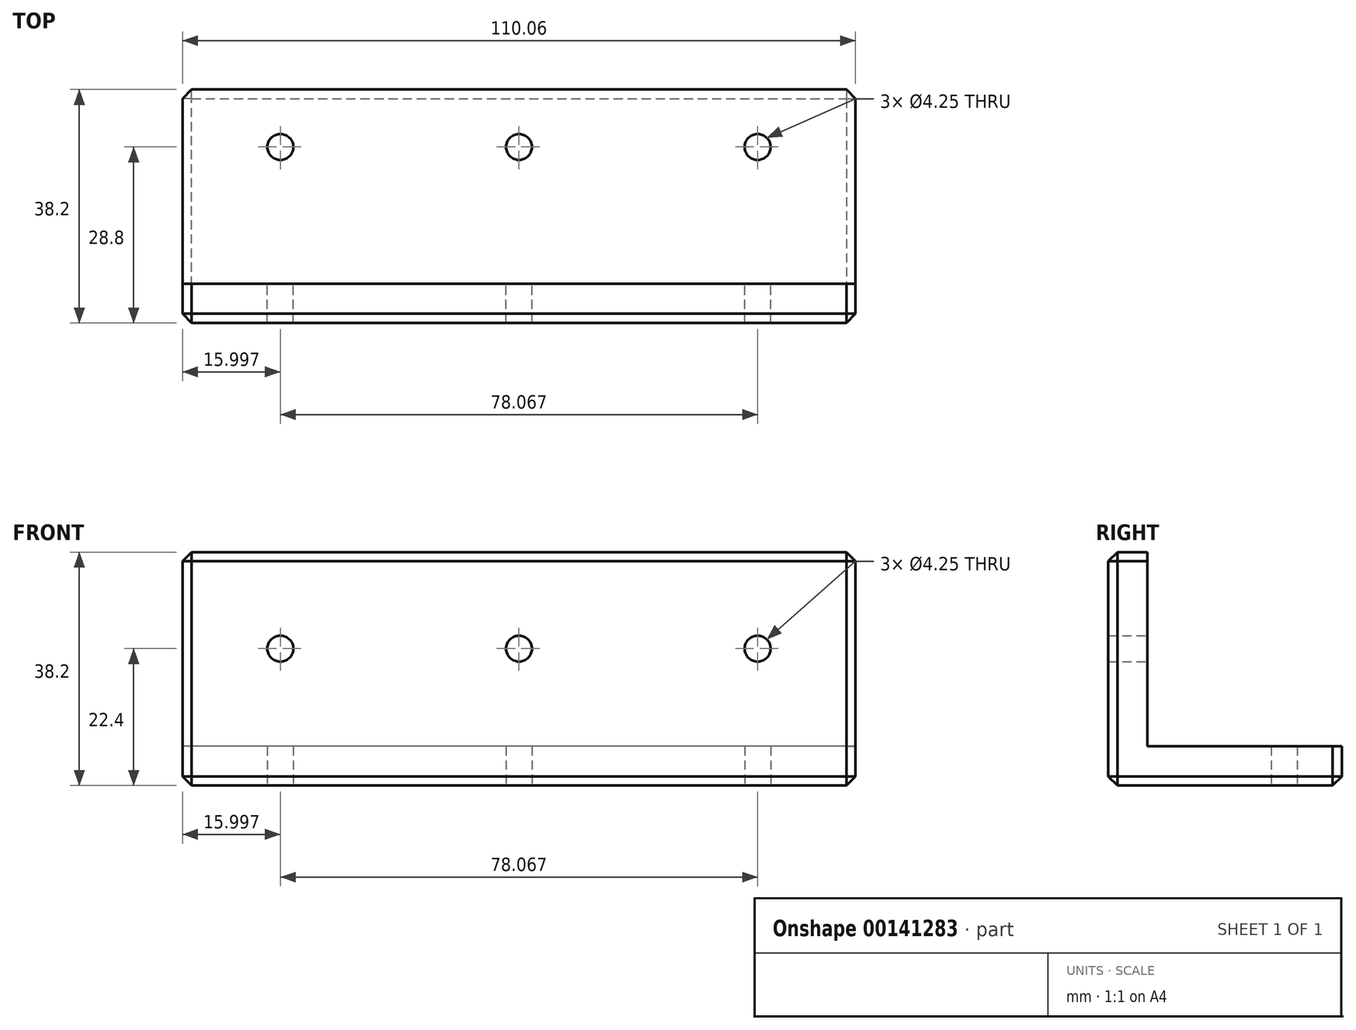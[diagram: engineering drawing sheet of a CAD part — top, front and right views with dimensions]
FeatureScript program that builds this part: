
annotation { "Feature Type Name" : "Feature", "Feature Type Description" : "" }
export const myFeature = defineFeature(function(context is Context, id is Id, definition is map)
    precondition{}
    {
        {
            var Q0;
            Q0=qCreatedBy(makeId("Top.planeOp"),FACE);
            var sketch = newSketch(context, id + "F0", { "sketchPlane" : qUnion([Q0])});
            skLineSegment(sketch, "E0.bottom", {"start": v(55.03, -15.9) * mm, "end": v(-55.03, -15.9) * mm});
            skLineSegment(sketch, "E0.top", {"start": v(55.03, 15.9) * mm, "end": v(-55.03, 15.9) * mm});
            skLineSegment(sketch, "E0.left", {"start": v(55.03, -15.9) * mm, "end": v(55.03, 15.9) * mm});
            skLineSegment(sketch, "E0.right", {"start": v(-55.03, -15.9) * mm, "end": v(-55.03, 15.9) * mm});
            skPoint(sketch, "E0.middle", {"position": v(0, 0) * mm});
            skLineSegment(sketch, "E1", {"start": v(-55.03, -9.5) * mm, "end": v(55.03, -9.5) * mm, "construction": true});
            skCircle(sketch, "E2", {"center": v(0, 6.5) * mm, "radius": 2.12 * mm});
            skCircle(sketch, "E3", {"center": v(-39.03, 6.5) * mm, "radius": 2.12 * mm});
            skCircle(sketch, "E4.MirrorC", {"center": v(39.03, 6.5) * mm, "radius": 2.12 * mm});
            skSolve(sketch);
        }
        {
            var Q0;
            Q0 = qSketchRegion(id + "F0", true);
            extrude(context, id + "F1", {"entities" : qUnion([Q0]), "depth" : 6.4 * mm});
        }
        {
            var Q0;
            Q0=makeQuery(id+"F1.opExtrude","SWEPT_FACE",FACE,{"disambiguationData":[OSD([sQuery(id+"F0.wireOp",EDGE,"E0.bottom")])]});
            var sketch = newSketch(context, id + "F2", { "sketchPlane" : qUnion([Q0])});
            skLineSegment(sketch, "E5.bottom", {"start": v(-55.03, 38.2) * mm, "end": v(55.03, 38.2) * mm});
            skLineSegment(sketch, "E5.top", {"start": v(-55.03, 0) * mm, "end": v(55.03, 0) * mm});
            skLineSegment(sketch, "E5.left", {"start": v(-55.03, 38.2) * mm, "end": v(-55.03, 0) * mm});
            skLineSegment(sketch, "E5.right", {"start": v(55.03, 38.2) * mm, "end": v(55.03, 0) * mm});
            skCircle(sketch, "E6", {"center": v(0, 22.4) * mm, "radius": 2.12 * mm});
            skCircle(sketch, "E7", {"center": v(-39.03, 22.4) * mm, "radius": 2.12 * mm});
            skCircle(sketch, "E8.MirrorC", {"center": v(39.03, 22.4) * mm, "radius": 2.12 * mm});
            skSolve(sketch);
        }
        {
            var Q0;
            Q0 = qSketchRegion(id + "F2", true);
            extrude(context, id + "F3", {"entities" : qUnion([Q0]), "operationType" : NewBodyOperationType.ADD, "depth" : 6.4 * mm});
        }
        {
            var Q0;
            Q0=makeQuery(id+"F3.opExtrude","CAP_EDGE",EDGE,{"disambiguationData":[OSD([sQuery(id+"F2.wireOp",EDGE,"E5.bottom")])],"isStart":false});
            var Q1;
            Q1=makeQuery(id+"F3.opExtrude","CAP_EDGE",EDGE,{"disambiguationData":[OSD([sQuery(id+"F2.wireOp",EDGE,"E5.top")])],"isStart":false});
            var Q2;
            Q2=makeQuery(id+"F1.opExtrude","CAP_EDGE",EDGE,{"disambiguationData":[OSD([sQuery(id+"F0.wireOp",EDGE,"E0.top")])],"isStart":true});
            var Q3;
            Q3=makeQuery(id+"F3.boolean.opBoolean","MERGE",EDGE,{"derivedFrom":[makeQuery(id+"F1.opExtrude","CAP_EDGE",EDGE,{"disambiguationData":[OSD([sQuery(id+"F0.wireOp",EDGE,"E0.left")])],"isStart":true}),makeQuery(id+"F3.opExtrude","SWEPT_EDGE",EDGE,{"disambiguationData":[OSD([sQuery(id+"F2.wireOp",EDGE,"E5.top"),sQuery(id+"F2.wireOp",EDGE,"E5.right")])]})]});
            var Q4;
            Q4=makeQuery(id+"F1.opExtrude","SWEPT_EDGE",EDGE,{"disambiguationData":[OSD([sQuery(id+"F0.wireOp",EDGE,"E0.top"),sQuery(id+"F0.wireOp",EDGE,"E0.left")])]});
            var Q5;
            Q5=makeQuery(id+"F1.opExtrude","SWEPT_EDGE",EDGE,{"disambiguationData":[OSD([sQuery(id+"F0.wireOp",EDGE,"E0.top"),sQuery(id+"F0.wireOp",EDGE,"E0.right")])]});
            var Q6;
            Q6=makeQuery(id+"F3.boolean.opBoolean","MERGE",EDGE,{"derivedFrom":[makeQuery(id+"F1.opExtrude","CAP_EDGE",EDGE,{"disambiguationData":[OSD([sQuery(id+"F0.wireOp",EDGE,"E0.right")])],"isStart":true}),makeQuery(id+"F3.opExtrude","SWEPT_EDGE",EDGE,{"disambiguationData":[OSD([sQuery(id+"F2.wireOp",EDGE,"E5.top"),sQuery(id+"F2.wireOp",EDGE,"E5.left")])]})]});
            var Q7;
            Q7=makeQuery(id+"F3.opExtrude","CAP_EDGE",EDGE,{"disambiguationData":[OSD([sQuery(id+"F2.wireOp",EDGE,"E5.left")])],"isStart":false});
            var Q8;
            Q8=makeQuery(id+"F3.opExtrude","CAP_EDGE",EDGE,{"disambiguationData":[OSD([sQuery(id+"F2.wireOp",EDGE,"E5.right")])],"isStart":false});
            var Q9;
            Q9=makeQuery(id+"F3.opExtrude","SWEPT_EDGE",EDGE,{"disambiguationData":[OSD([sQuery(id+"F2.wireOp",EDGE,"E5.bottom"),sQuery(id+"F2.wireOp",EDGE,"E5.left")])]});
            var Q10;
            Q10=makeQuery(id+"F3.opExtrude","SWEPT_EDGE",EDGE,{"disambiguationData":[OSD([sQuery(id+"F2.wireOp",EDGE,"E5.bottom"),sQuery(id+"F2.wireOp",EDGE,"E5.right")])]});
            chamfer(context, id + "F4", {"entities" : qUnion([Q0, Q1, Q2, Q3, Q4, Q5, Q6, Q7, Q8, Q9, Q10]), "width" : 1.5 * mm, "tangentPropagation" : true});
        }
    });
